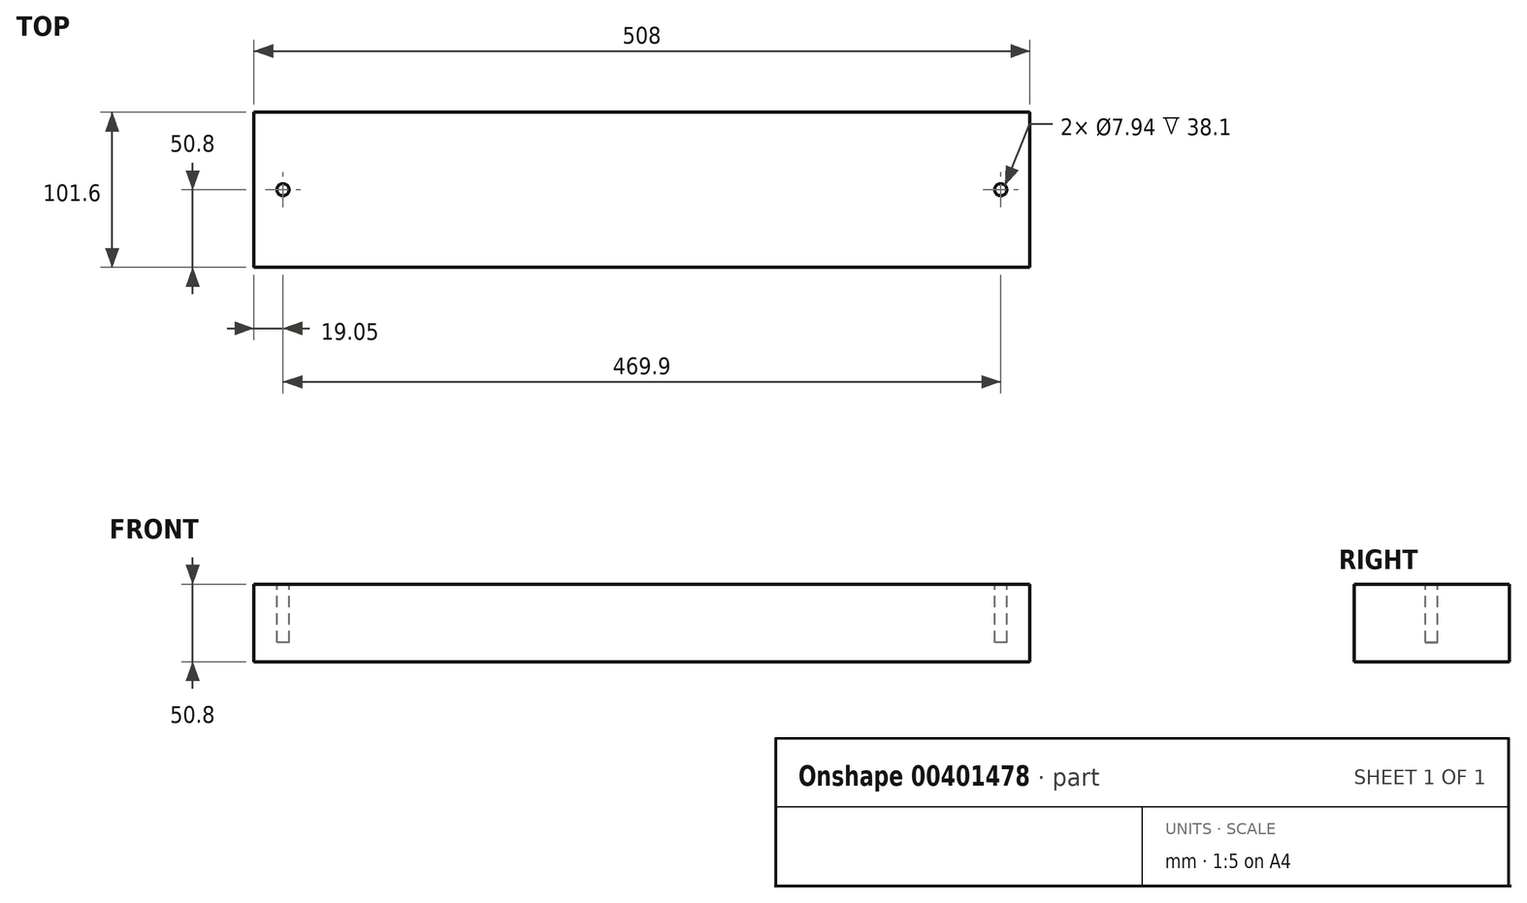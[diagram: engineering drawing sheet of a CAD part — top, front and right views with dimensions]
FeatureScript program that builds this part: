
annotation { "Feature Type Name" : "Feature", "Feature Type Description" : "" }
export const myFeature = defineFeature(function(context is Context, id is Id, definition is map)
    precondition{}
    {
        {
            var Q0;
            Q0=qCreatedBy(makeId("Top.planeOp"),FACE);
            var sketch = newSketch(context, id + "F0", { "sketchPlane" : qUnion([Q0])});
            skLineSegment(sketch, "E0.bottom", {"start": v(254, 50.8) * mm, "end": v(-254, 50.8) * mm});
            skLineSegment(sketch, "E0.top", {"start": v(254, -50.8) * mm, "end": v(-254, -50.8) * mm});
            skLineSegment(sketch, "E0.left", {"start": v(254, 50.8) * mm, "end": v(254, -50.8) * mm});
            skLineSegment(sketch, "E0.right", {"start": v(-254, 50.8) * mm, "end": v(-254, -50.8) * mm});
            skPoint(sketch, "E0.middle", {"position": v(0, 0) * mm});
            skLineSegment(sketch, "E1", {"start": v(-254, 50.8) * mm, "end": v(0, 50.8) * mm});
            skSolve(sketch);
        }
        {
            var Q0;
            Q0 = qSketchRegion(id + "F0", true);
            extrude(context, id + "F1", {"entities" : qUnion([Q0]), "oppositeDirection" : true, "depth" : 50.8 * mm});
        }
        {
            var Q0;
            Q0=qCreatedBy(makeId("Top.planeOp"),FACE);
            var sketch = newSketch(context, id + "F2", { "sketchPlane" : qUnion([Q0])});
            skCircle(sketch, "E2", {"center": v(-234.95, 0) * mm, "radius": 3.97 * mm});
            skCircle(sketch, "E3", {"center": v(234.95, 0) * mm, "radius": 3.97 * mm});
            skSolve(sketch);
        }
        {
            var Q0;
            Q0 = qSketchRegion(id + "F2", true);
            extrude(context, id + "F3", {"entities" : qUnion([Q0]), "operationType" : NewBodyOperationType.REMOVE, "oppositeDirection" : true, "depth" : 38.1 * mm});
        }
    });
